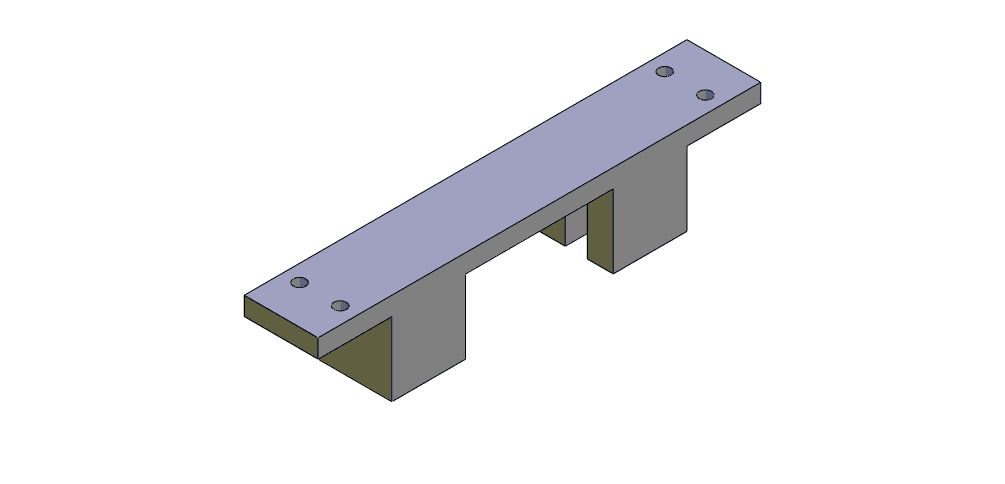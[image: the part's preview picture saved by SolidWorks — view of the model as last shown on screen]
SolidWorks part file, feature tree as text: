
SOLIDWORKS PART (.sldprt)
format: sldprt  version: not decoded by parser v0  size: 266,752 bytes
history: native  units: mm
features: sketch x11, extrude x5, cut_extrude x2, hole x2, material x1 (+12 scaffold rows collapsed)
feature tree (33):
  scaffold x12  (default folders/planes/origin — collapsed)
  material  "Material <not specified>"
  sketch  "Sketch1"  dims[D1=20.0mm D2=40.0mm]
  extrude  "Boss-Extrude1"  Depth=5mm
  sketch  "Sketch2"  dims[D1=20.0mm]
  extrude  "Boss-Extrude2"  Depth=20mm
  sketch  "Sketch3"  dims[D1=6.0mm D2=16.0mm D3=7.0mm]
  cut_extrude  "Cut-Extrude1"  Depth=20mm
  hole  "M3 Clearance Hole1"  Diameter=3.4mm Depth=4.999mm
  sketch  "Sketch5"  dims[D1=9.5mm D2=9.5mm D3=4.5mm D4=4.5mm]
  sketch  "Sketch4"  dims[hole-wizard template sketch: 47 standard entries collapsed; hole parameters kept: c15.Hole Depth=4.999mm c15.D3=~14.816244mm c15.Drill Angle=118.0deg]
  sketch  "Sketch6"
  extrude  "Boss-Extrude3"  Depth=60mm
  sketch  "Sketch7"
  extrude  "Boss-Extrude4"  Depth=20mm
  sketch  "Sketch8"  dims[D1=20.0mm D2=20.0mm]
  extrude  "Boss-Extrude5"  Depth=20mm
  sketch  "Sketch9"  dims[c1.D1=4.0mm c1.D2=7.0mm c1.D3=7.0mm c2.D1=7.0mm c2.D2=7.0mm c2.D3=4.0mm c2.D4=20.0mm]
  cut_extrude  "Cut-Extrude2"  Depth=20mm
  hole  "M3 Clearance Hole2"  Diameter=3.4mm Depth=5mm
  sketch  "Sketch11"  dims[D1=9.5mm D2=9.5mm D3=4.5mm D4=4.5mm]
  sketch  "Sketch10"  dims[hole-wizard template sketch: 61 standard entries collapsed; hole parameters above]
decode coverage: 18 of 20 modeling features carry decoded parameters
note: ~ marks probable driven/reference dimensions
note: suppression state not decoded; provenance and decode notes live in map.json
